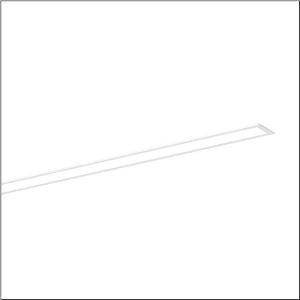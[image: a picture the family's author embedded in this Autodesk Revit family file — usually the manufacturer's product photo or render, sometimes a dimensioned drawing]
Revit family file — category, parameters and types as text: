
# Revit family: silica_r__21_51mx10db32wb_8ee9
name_source: partatom
category: Lighting Fixtures
units: mm (PartAtom-declared; Revit-internal decimal feet)

## family parameters
Cut with Voids When Loaded = No
Host = Face
Light Source = No
Part Type = Normal
Room Calculation Point = No
Round Connector Dimension = Use Diameter
Shared = No

## types (1)
- --- (1 x LED, 3000 lm, 20.2 W, 3000K)
    Apparent Load = 20 VA
    CIE Flux Codes = 48 79 96 100 100
    Color Rendering = 80
    Color Temperature = 3000K
    Default Elevation = 1800 mm
    Description = Silica® 21, office luminaire, primary optical cover: cover, of PMMA, opal, light emission: direct distribution, primary light characteristic: symmetric, installation type: recessed, LED, rated luminous flux: 3.000lm, luminous efficacy: 149lm/W, light colour: 830, colour temperature: 3000K, with terminal, 3+2-pole, max. 2.5mm², mains connection: 220..240V, AC, 50/60Hz, luminaire housing, of aluminium, traffic white (RAL 9016), length: 1.528mm, width: 79mm, height: 53mm, protection rating (complete): IP20, insulation class (complete): insulation class I (protective earthing), certification: CE, permissible operating ambient temperature: 0..+35°C, standard: EN 50419, packaging unit: 1 piece
    Height = 0 mm  [stored 0 ft]
    Lamp = 1 x LED
    Lamp Light Flux = 3000 lm
    Lamp Power = 20.2 W
    Lamp count = 1
    Length = 1527 mm
    Luminous efficacy = 149 lm/W
    Manufacturer = Siteco
    ModVariant = No
    Model = 51MX10DB32WB
    Mounting Place = Ceiling
    Mounting Type = Recessed
    Number of Poles = 1
    OnlyDefault = Yes
    Power Factor = 1
    Product Name = Silica® 21
    Product group = office luminaire | ceiling recessed
    ProductGroupID = 401
    Protection Class = Protection class I
    Protection Degree = IP 20
    RLX_Detail_Level = 1
    RLX_Emergency_Light_Flux = 0 lm
    RLX_Emergency_Type = 0
    RLX_Emergency_Type_DB = No
    RlxData = <blob elided: 20873 chars, md5=429c9102>
    Socket = socket
    Standby Power = 0 W
    System Light Flux = 3000 lm
    System Power = 20 W
    Type Comments = factory setting: luminous flux: 100 % | dim-lin: 254 | 233 mA
    Type Image = l_1313615.jpg
    URL = http://relux.com
    VarID = @adj_065835
    Voltage = 0 V
    Weight = 0.00 kg
    Width = 79 mm

note: [stored X ft] marks values corroborated as IEEE doubles in the binary element streams (Revit-internal decimal feet)

## geometry (parser evidence)
native form markers: Blend x4, Sweep x11
no freeform markers — native parametric forms only
